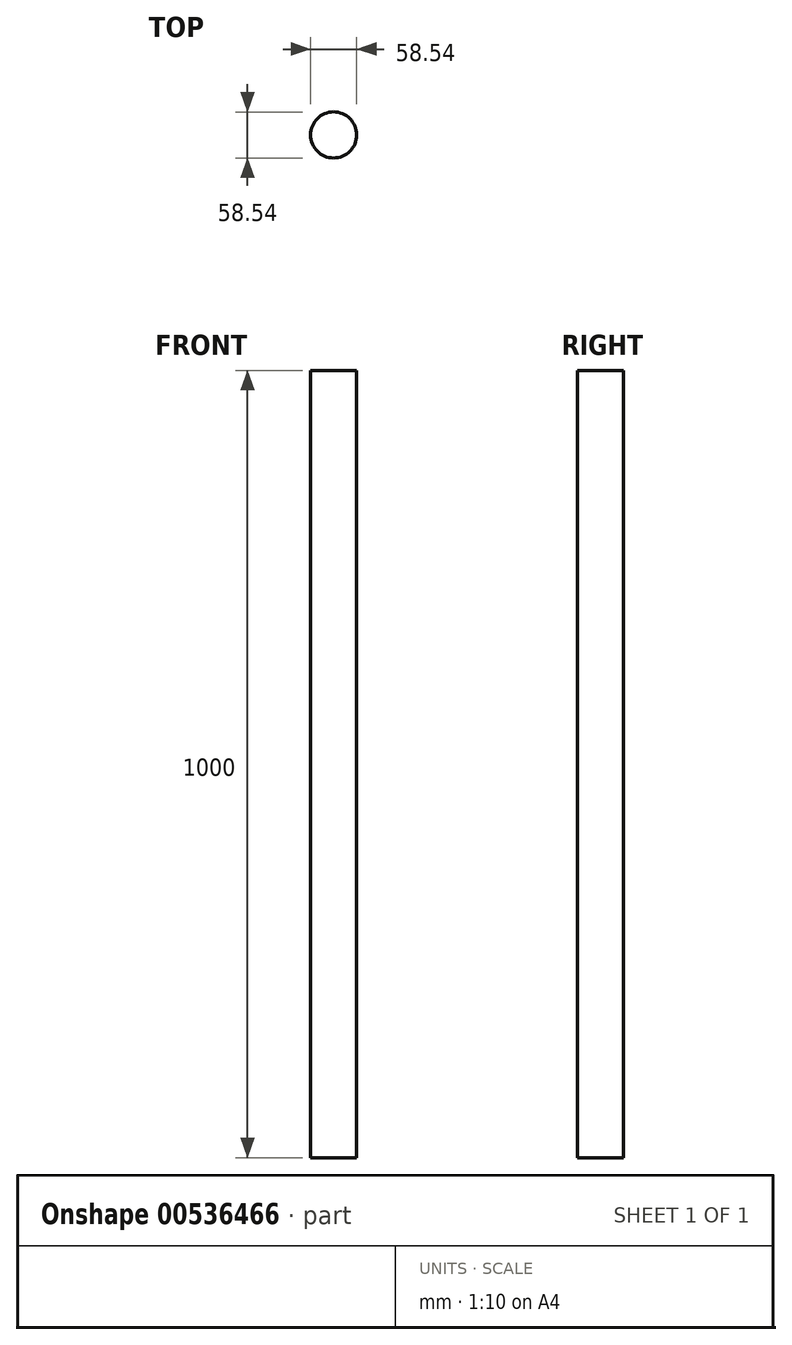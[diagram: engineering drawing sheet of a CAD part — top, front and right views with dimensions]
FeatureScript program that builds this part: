
annotation { "Feature Type Name" : "Feature", "Feature Type Description" : "" }
export const myFeature = defineFeature(function(context is Context, id is Id, definition is map)
    precondition{}
    {
        {
            var Q0;
            Q0=qCreatedBy(makeId("Top.planeOp"),FACE);
            var sketch = newSketch(context, id + "F0", { "sketchPlane" : qUnion([Q0])});
            skCircle(sketch, "E0", {"center": v(0, 0) * mm, "radius": 29.27 * mm});
            skSolve(sketch);
        }
        {
            var Q0;
            Q0 = qSketchRegion(id + "F0", true);
            extrude(context, id + "F1", {"entities" : qUnion([Q0]), "depth" : 1000 * mm, "offsetDistance" : 25 * mm});
        }
    });
